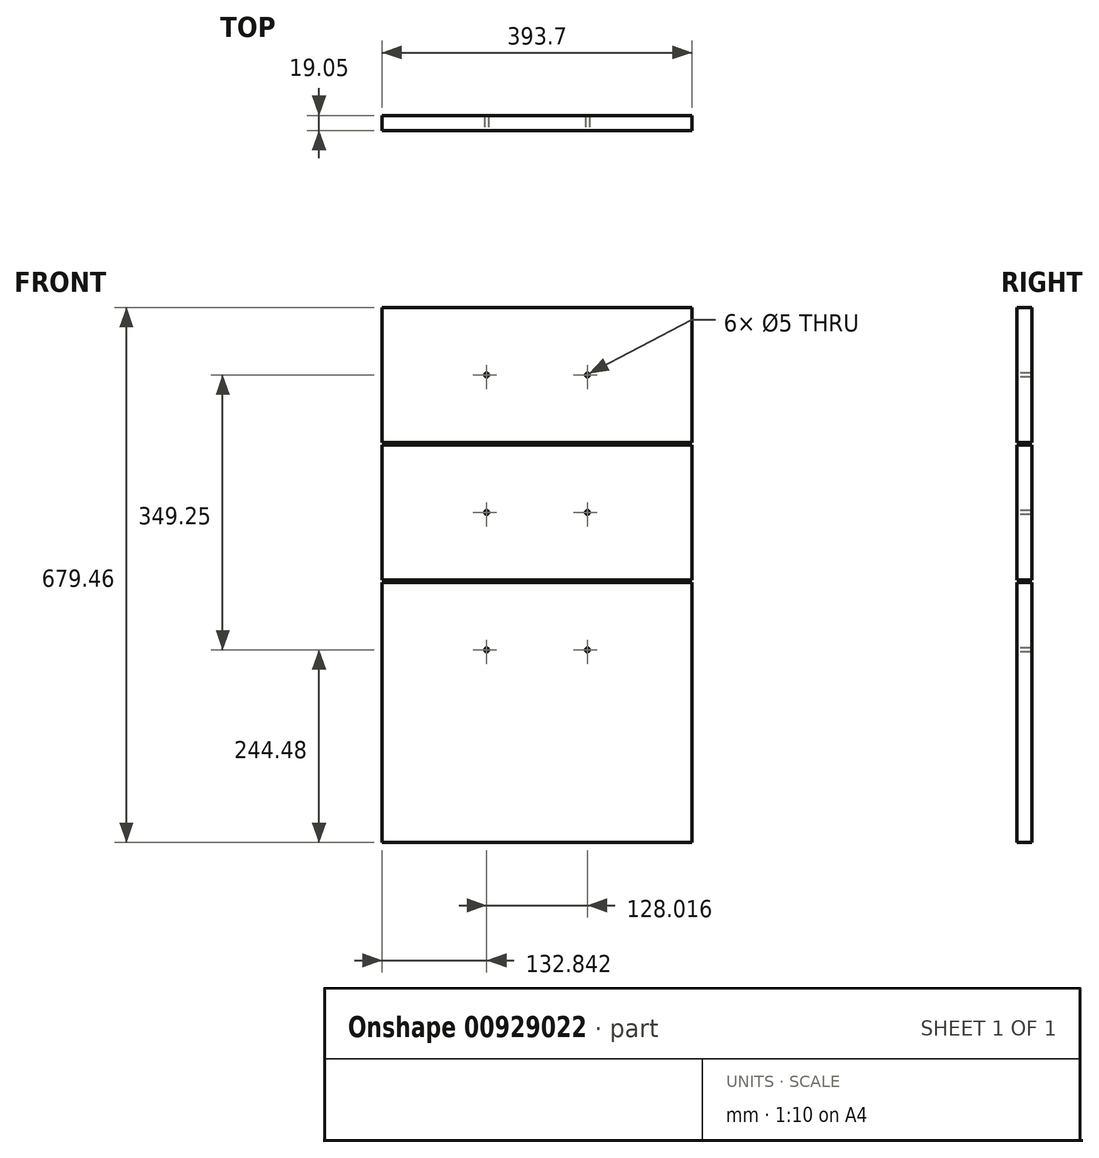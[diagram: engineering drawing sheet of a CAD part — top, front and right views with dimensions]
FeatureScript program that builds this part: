
annotation { "Feature Type Name" : "Feature", "Feature Type Description" : "" }
export const myFeature = defineFeature(function(context is Context, id is Id, definition is map)
    precondition{}
    {
        {
            var Q0;
            Q0=qCreatedBy(makeId("Front.planeOp"),FACE);
            var sketch = newSketch(context, id + "F0", { "sketchPlane" : qUnion([Q0])});
            skLineSegment(sketch, "E0.bottom", {"start": v(196.85, 339.73) * mm, "end": v(-196.85, 339.73) * mm});
            skLineSegment(sketch, "E0.top", {"start": v(196.85, -339.73) * mm, "end": v(-196.85, -339.73) * mm});
            skLineSegment(sketch, "E0.left", {"start": v(196.85, 339.73) * mm, "end": v(196.85, -339.73) * mm});
            skLineSegment(sketch, "E0.right", {"start": v(-196.85, 339.73) * mm, "end": v(-196.85, -339.73) * mm});
            skPoint(sketch, "E0.middle", {"position": v(0, 0) * mm});
            skSolve(sketch);
        }
        {
            var Q0;
            Q0=makeQuery(id+"F0.imprint","IMPRINT",FACE,{"disambiguationData":[TD([[makeQuery(id+"F0.imprint","IMPRINT",EDGE,{"derivedFrom":sQuery(id+"F0.wireOp",EDGE,"E0.bottom")}),1.0]])]});
            extrude(context, id + "F1", {"entities" : qUnion([Q0]), "depth" : 19.05 * mm, "offsetDistance" : 25.4 * mm});
        }
        {
            var Q0;
            Q0=makeQuery(id+"F1.opExtrude","CAP_FACE",FACE,{"disambiguationData":[OSD([sQuery(id+"F0.wireOp",EDGE,"E0.bottom"),sQuery(id+"F0.wireOp",EDGE,"E0.top"),sQuery(id+"F0.wireOp",EDGE,"E0.left"),sQuery(id+"F0.wireOp",EDGE,"E0.right")])],"isStart":false});
            var sketch = newSketch(context, id + "F2", { "sketchPlane" : qUnion([Q0])});
            skLineSegment(sketch, "E1", {"start": v(-196.85, -339.73) * mm, "end": v(-196.85, -9.52) * mm});
            skLineSegment(sketch, "E2", {"start": v(-196.85, -9.52) * mm, "end": v(196.85, -9.52) * mm});
            skLineSegment(sketch, "E3", {"start": v(-196.85, -9.52) * mm, "end": v(-196.85, -6.35) * mm});
            skLineSegment(sketch, "E4", {"start": v(-196.85, -6.35) * mm, "end": v(196.85, -6.35) * mm});
            skLineSegment(sketch, "E5.bottom", {"start": v(196.85, 168.28) * mm, "end": v(-196.85, 168.28) * mm});
            skLineSegment(sketch, "E5.top", {"start": v(196.85, 165.1) * mm, "end": v(-196.85, 165.1) * mm});
            skLineSegment(sketch, "E5.left", {"start": v(196.85, 168.28) * mm, "end": v(196.85, 165.1) * mm});
            skLineSegment(sketch, "E5.right", {"start": v(-196.85, 168.28) * mm, "end": v(-196.85, 165.1) * mm});
            skPoint(sketch, "E5.middle", {"position": v(0, 166.69) * mm});
            skSolve(sketch);
        }
        {
            var Q0;
            Q0=makeQuery(id+"F2.imprint","IMPRINT",FACE,{"disambiguationData":[TD([[makeQuery(id+"F2.imprint","IMPRINT",EDGE,{"derivedFrom":sQuery(id+"F2.wireOp",EDGE,"E5.bottom")}),1.0]])]});
            var Q1;
            {var subQ0=sQuery(id+"F2.wireOp",EDGE,"E2");Q1=makeQuery(id+"F2.imprint","IMPRINT",FACE,{"disambiguationData":[TD([[makeQuery(id+"F2.imprint","IMPRINT",EDGE,{"derivedFrom":subQ0}),1.0]])]});}
            extrude(context, id + "F3", {"entities" : qUnion([Q0, Q1]), "operationType" : NewBodyOperationType.REMOVE, "oppositeDirection" : true, "depth" : 25.4 * mm, "offsetDistance" : 25.4 * mm});
        }
        {
            var Q0;
            {var subQ0=sQuery(id+"F0.wireOp",EDGE,"E0.bottom");var subQ1=sQuery(id+"F0.wireOp",EDGE,"E0.right");var subQ2=sQuery(id+"F0.wireOp",EDGE,"E0.left");Q0=makeQuery(id+"F3.boolean.opBoolean","SPLIT",FACE,{"disambiguationData":[TD([makeQuery(id+"F1.opExtrude","SWEPT_FACE",FACE,{"disambiguationData":[OSD([subQ0])]})])],"derivedFrom":makeQuery(id+"F1.opExtrude","CAP_FACE",FACE,{"disambiguationData":[OSD([subQ0,sQuery(id+"F0.wireOp",EDGE,"E0.top"),subQ2,subQ1])],"isStart":false})});}
            var sketch = newSketch(context, id + "F4", { "sketchPlane" : qUnion([Q0])});
            skLineSegment(sketch, "E6", {"start": v(0, 254) * mm, "end": v(-64, 254) * mm});
            skPoint(sketch, "E6.startSnap0", {"position": v(-196.85, 254) * mm});
            skPoint(sketch, "E6.startSnap1", {"position": v(0, 339.73) * mm});
            skLineSegment(sketch, "E7", {"start": v(-64, 254) * mm, "end": v(64, 254) * mm});
            skSolve(sketch);
        }
        {
            var Q0;
            Q0=sQuery(id+"F4.wireOp",VERTEX,"E6.end");
            var Q1;
            Q1=sQuery(id+"F4.wireOp",VERTEX,"E7.end");
            var Q2;
            Q2=makeQuery(id+"F3.boolean.opBoolean","SPLIT",BODY,{"disambiguationData":[OD(0.0)],"derivedFrom":makeQuery(id+"F1.opExtrude","SWEPT_BODY",BODY,{"disambiguationData":[OSD([sQuery(id+"F0.wireOp",EDGE,"E0.bottom"),sQuery(id+"F0.wireOp",EDGE,"E0.top"),sQuery(id+"F0.wireOp",EDGE,"E0.left"),sQuery(id+"F0.wireOp",EDGE,"E0.right")])]})});
            hole(context, id + "F5", {"style" : HoleStyle.SIMPLE, "endStyle" : HoleEndStyle.THROUGH, "holeDiameter" : 5 * mm, "majorDiameter" : 6.35 * mm, "isTappedThrough" : true, "tappedDepth" : 12.7 * mm, "tapClearance" : 3, "startFromSketch" : true, "locations" : qUnion([Q0, Q1]), "scope" : qUnion([Q2])});
        }
        {
            var Q0;
            {var subQ0=sQuery(id+"F0.wireOp",EDGE,"E0.left");var subQ1=sQuery(id+"F0.wireOp",EDGE,"E0.right");Q0=makeQuery(id+"F3.boolean.opBoolean","SPLIT",FACE,{"disambiguationData":[TD([makeQuery(id+"F3.opExtrude","SWEPT_FACE",FACE,{"disambiguationData":[OSD([sQuery(id+"F2.wireOp",EDGE,"E4")])]})])],"derivedFrom":makeQuery(id+"F1.opExtrude","CAP_FACE",FACE,{"disambiguationData":[OSD([sQuery(id+"F0.wireOp",EDGE,"E0.bottom"),sQuery(id+"F0.wireOp",EDGE,"E0.top"),subQ0,subQ1])],"isStart":false})});}
            var sketch = newSketch(context, id + "F6", { "sketchPlane" : qUnion([Q0])});
            skLineSegment(sketch, "E8", {"start": v(0, 79.38) * mm, "end": v(64, 79.38) * mm});
            skPoint(sketch, "E8.startSnap0", {"position": v(-196.85, 79.38) * mm});
            skLineSegment(sketch, "E9", {"start": v(64, 79.38) * mm, "end": v(-64, 79.38) * mm});
            skSolve(sketch);
        }
        {
            var Q0;
            Q0=sQuery(id+"F6.wireOp",VERTEX,"E9.end");
            var Q1;
            Q1=sQuery(id+"F6.wireOp",VERTEX,"E8.end");
            var Q2;
            Q2=makeQuery(id+"F3.boolean.opBoolean","SPLIT",BODY,{"disambiguationData":[OD(2.0)],"derivedFrom":makeQuery(id+"F1.opExtrude","SWEPT_BODY",BODY,{"disambiguationData":[OSD([sQuery(id+"F0.wireOp",EDGE,"E0.bottom"),sQuery(id+"F0.wireOp",EDGE,"E0.top"),sQuery(id+"F0.wireOp",EDGE,"E0.left"),sQuery(id+"F0.wireOp",EDGE,"E0.right")])]})});
            hole(context, id + "F7", {"style" : HoleStyle.SIMPLE, "endStyle" : HoleEndStyle.THROUGH, "holeDiameter" : 5 * mm, "majorDiameter" : 6.35 * mm, "isTappedThrough" : true, "tappedDepth" : 12.7 * mm, "tapClearance" : 3, "startFromSketch" : true, "locations" : qUnion([Q0, Q1]), "scope" : qUnion([Q2])});
        }
        {
            var Q0;
            {var subQ0=sQuery(id+"F0.wireOp",EDGE,"E0.top");var subQ1=sQuery(id+"F0.wireOp",EDGE,"E0.left");var subQ2=sQuery(id+"F0.wireOp",EDGE,"E0.right");Q0=makeQuery(id+"F3.boolean.opBoolean","SPLIT",FACE,{"disambiguationData":[TD([makeQuery(id+"F1.opExtrude","SWEPT_FACE",FACE,{"disambiguationData":[OSD([subQ0])]})])],"derivedFrom":makeQuery(id+"F1.opExtrude","CAP_FACE",FACE,{"disambiguationData":[OSD([sQuery(id+"F0.wireOp",EDGE,"E0.bottom"),subQ0,subQ1,subQ2])],"isStart":false})});}
            var sketch = newSketch(context, id + "F8", { "sketchPlane" : qUnion([Q0])});
            skLineSegment(sketch, "E10", {"start": v(0, -9.52) * mm, "end": v(0, -95.25) * mm});
            skLineSegment(sketch, "E11", {"start": v(0, -95.25) * mm, "end": v(64, -95.25) * mm});
            skLineSegment(sketch, "E12", {"start": v(64, -95.25) * mm, "end": v(-64, -95.25) * mm});
            skPoint(sketch, "E12.endSnap0", {"position": v(32, -95.25) * mm});
            skSolve(sketch);
        }
        {
            var Q0;
            Q0=sQuery(id+"F8.wireOp",VERTEX,"E11.end");
            var Q1;
            Q1=sQuery(id+"F8.wireOp",VERTEX,"E12.end");
            var Q2;
            Q2=makeQuery(id+"F3.boolean.opBoolean","SPLIT",BODY,{"disambiguationData":[OD(1.0)],"derivedFrom":makeQuery(id+"F1.opExtrude","SWEPT_BODY",BODY,{"disambiguationData":[OSD([sQuery(id+"F0.wireOp",EDGE,"E0.bottom"),sQuery(id+"F0.wireOp",EDGE,"E0.top"),sQuery(id+"F0.wireOp",EDGE,"E0.left"),sQuery(id+"F0.wireOp",EDGE,"E0.right")])]})});
            hole(context, id + "F9", {"style" : HoleStyle.SIMPLE, "endStyle" : HoleEndStyle.THROUGH, "holeDiameter" : 5 * mm, "majorDiameter" : 6.35 * mm, "isTappedThrough" : true, "tappedDepth" : 12.7 * mm, "tapClearance" : 3, "startFromSketch" : true, "locations" : qUnion([Q0, Q1]), "scope" : qUnion([Q2])});
        }
    });
